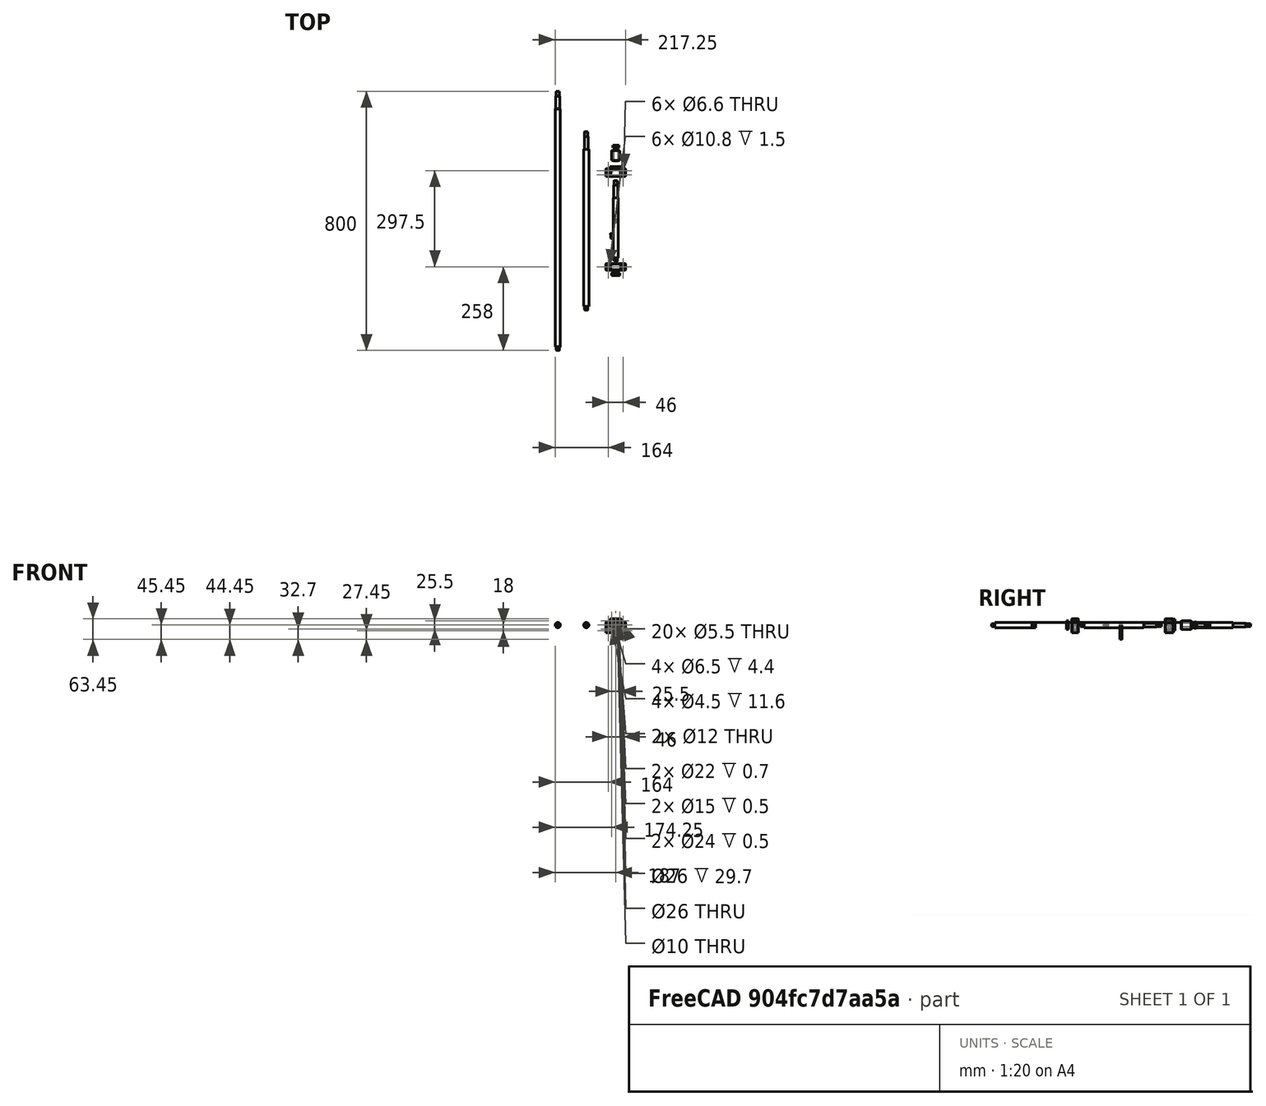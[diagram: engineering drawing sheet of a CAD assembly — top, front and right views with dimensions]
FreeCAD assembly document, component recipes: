
FREECAD ASSEMBLY — COMPONENT RECIPES ("Ballscrew")

This assembly document has 14 components, labeled P0..P13 below (a component is one placed body or linked part). 8 of them carry a construction recipe — the FreeCAD feature program that regenerates the part from scratch, quoted from this document or its linked companion documents; the rest are supplied as boundary geometry only. No exploded tour is included for this assembly.
COMPONENT P0 — recipe-attached ("Link(6000Z)", modeled in this document).
Construction recipe (the document's own serialized feature program — sketch geometry with constraints, then the solid features built on it; lengths are millimeters unless a unit is written):

FEATURE [Sketcher::SketchObject] Sketch002
  FullyConstrained = true
  MapMode = 5
  Placement = pos=(0,0,0) rot=(0.57735,0.57735,0.57735;2.0944rad)
  Support = -> [YZ_Plane001]
  sketch-geometry (21):
    g0: LineSegment StartX=-3.5 StartY=13 StartZ=0 EndX=3.5 EndY=13 EndZ=0
    g1: LineSegment StartX=3.5 StartY=13 StartZ=0 EndX=3.5 EndY=11 EndZ=0
    g2: LineSegment StartX=3.5 StartY=5 StartZ=0 EndX=-3.5 EndY=5 EndZ=0
    g3: LineSegment StartX=-3.5 StartY=5 StartZ=0 EndX=-3.5 EndY=7 EndZ=0
    g4: LineSegment StartX=-3.5 StartY=11 StartZ=0 EndX=-2.5 EndY=11 EndZ=0
    g5: LineSegment StartX=-2.5 StartY=11 StartZ=0 EndX=-2.5 EndY=10.5 EndZ=0
    g6: LineSegment StartX=-2.5 StartY=10.5 StartZ=0 EndX=-3 EndY=10.5 EndZ=0
    g7: LineSegment StartX=-3 StartY=10.5 StartZ=0 EndX=-3 EndY=7.5 EndZ=0
    g8: LineSegment StartX=-3 StartY=7.5 StartZ=0 EndX=-2.5 EndY=7.5 EndZ=0
    g9: LineSegment StartX=-2.5 StartY=7.5 StartZ=0 EndX=-2.5 EndY=7 EndZ=0
    g10: LineSegment StartX=-2.5 StartY=7 StartZ=0 EndX=-3.5 EndY=7 EndZ=0
    g11: LineSegment StartX=-3.5 StartY=11 StartZ=0 EndX=-3.5 EndY=13 EndZ=0
    g12: LineSegment StartX=3.5 StartY=11 StartZ=0 EndX=2.5 EndY=11 EndZ=0
    g13: LineSegment StartX=2.5 StartY=11 StartZ=0 EndX=2.5 EndY=10.5 EndZ=0
    g14: LineSegment StartX=2.5 StartY=10.5 StartZ=0 EndX=3 EndY=10.5 EndZ=0
    g15: LineSegment StartX=3 StartY=10.5 StartZ=0 EndX=3 EndY=7.5 EndZ=0
    g16: LineSegment StartX=3 StartY=7.5 StartZ=0 EndX=2.5 EndY=7.5 EndZ=0
    g17: LineSegment StartX=2.5 StartY=7.5 StartZ=0 EndX=2.5 EndY=7 EndZ=0
    g18: LineSegment StartX=2.5 StartY=7 StartZ=0 EndX=3.5 EndY=7 EndZ=0
    g19: LineSegment StartX=3.5 StartY=7 StartZ=0 EndX=3.5 EndY=5 EndZ=0
    g20: GeomPoint [constr] X=0 Y=5 Z=0
  constraints (59):
    c: Coincident(g0,g1)
    c: Coincident(g19,g2)
    c: Coincident(g2,g3)
    c: Coincident(g11,g0)
    c: Horizontal(g0)
    c: Horizontal(g2)
    c: Vertical(g1)
    c: Vertical(g3)
    c: DistanceX(g2,g2) = 7
    c: DistanceY(g-1,g0) = 13
    c: Horizontal(g4)
    c: Coincident(g4,g5)
    c: Coincident(g5,g6)
    c: Coincident(g6,g7)
    c: Vertical(g7)
    c: Coincident(g7,g8)
    c: Horizontal(g8)
    c: Coincident(g8,g9)
    c: Vertical(g9)
    c: Coincident(g9,g10)
    c: Horizontal(g10)
    c: Coincident(g3,g10)
    c: Coincident(g11,g4)
    c: Tangent(g3,g11)
    c: Equal(g8,g6)
    c: Horizontal(g6)
    c: Vertical(g5)
    c: Equal(g5,g9)
    c: DistanceX(g6,g6) = 0.5
    c: DistanceX(g4,g4) = 1
    c: Equal(g3,g11)
    c: DistanceY(g11,g11) = 2
    c: DistanceY(g5,g5) = 0.5
    c: Horizontal(g12)
    c: Coincident(g12,g13)
    c: Vertical(g13)
    c: Coincident(g13,g14)
    c: Coincident(g14,g15)
    c: Vertical(g15)
    c: Coincident(g15,g16)
    c: Horizontal(g16)
    c: Coincident(g16,g17)
    c: Vertical(g17)
    c: Coincident(g17,g18)
    c: Horizontal(g18)
    c: Coincident(g1,g12)
    c: Coincident(g19,g18)
    c: Tangent(g1,g19)
    c: Equal(g12,g4)
    c: Equal(g4,g18)
    c: Equal(g16,g14)
    c: Equal(g14,g6)
    c: Equal(g13,g17)
    c: Equal(g17,g9)
    c: Horizontal(g17,g9)
    c: Horizontal(g12,g4)
    c: PointOnObject(g20,g-2)
    c: Symmetric(g2,g2,g20)
    c: DistanceY(g-1,g2) = 5
FEATURE [PartDesign::Revolution] Revolution
  Angle = 360
  Axis = (1e-16,1,-1e-16)
  Base = (0,0,0)
  ClaimChildren = false
  Fit = 0
  FitJoin = 0
  InnerFit = 0
  InnerFitJoin = 0
  NewSolid = false
  Placement = pos=(0,0,0) rot=(0.57735,0.57735,0.57735;2.0944rad)
  Profile = -> Sketch002
  ReferenceAxis = -> Y_Axis001
  Refine = true
  Suppress = false
FEATURE [PartDesign::Chamfer] Chamfer001
  Angle = 45
  Base = -> Revolution [Edge2,Edge3,Edge18,Edge17,Edge15,Edge5,Edge1,Edge20]
  BaseFeature = -> Revolution
  ChamferType = 0
  FlipDirection = false
  NewSolid = false
  Placement = pos=(0,0,0) rot=(0.57735,0.57735,0.57735;2.0944rad)
  Refine = true
  Size = 0.3
  Size2 = 1
  SupportTransform = false
  Suppress = false
FEATURE [PartDesign::Body] Body001  label="6000Z"
  AutoGroupSolids = false
  ExportMode = 0
  Group = -> [Sketch002,Revolution,Chamfer001]
  Origin = -> Origin001
  Placement = pos=(0,-165,0) rot=(0,0,1;0rad)
  Tip = -> Chamfer001
  _ExportChildren = -> [Revolution,Chamfer001]
  _GroupVersion = 1
COMPONENT P1 — recipe-attached ("Link001(BF12)", modeled in this document).
Construction recipe (the document's own serialized feature program — sketch geometry with constraints, then the solid features built on it; lengths are millimeters unless a unit is written):

FEATURE [Sketcher::SketchObject] Sketch
  FullyConstrained = true
  MapMode = 5
  Placement = pos=(0,0,0) rot=(1,0,0;1.5708rad)
  Support = -> [XZ_Plane]
  sketch-geometry (18):
    g0: LineSegment StartX=-30.25 StartY=33 StartZ=0 EndX=-16.75 EndY=33 EndZ=0
    g1: LineSegment StartX=30.25 StartY=33 StartZ=0 EndX=30.25 EndY=0 EndZ=0
    g2: LineSegment StartX=30.25 StartY=0 StartZ=0 EndX=-30.25 EndY=0 EndZ=0
    g3: LineSegment StartX=-30.25 StartY=0 StartZ=0 EndX=-30.25 EndY=33 EndZ=0
    g4: LineSegment StartX=-16.75 StartY=43 StartZ=0 EndX=16.75 EndY=43 EndZ=0
    g5: LineSegment StartX=16.75 StartY=43 StartZ=0 EndX=16.75 EndY=33 EndZ=0
    g6: LineSegment StartX=-16.75 StartY=33 StartZ=0 EndX=-16.75 EndY=43 EndZ=0
    g7: Circle CenterX=-23 CenterY=25 CenterZ=0 NormalX=0 NormalY=0 NormalZ=1 AngleXU=0 Radius=2.75
    g8: Circle CenterX=-23 CenterY=7 CenterZ=0 NormalX=0 NormalY=0 NormalZ=1 AngleXU=0 Radius=2.75
    g9: Circle CenterX=23 CenterY=25 CenterZ=0 NormalX=0 NormalY=0 NormalZ=1 AngleXU=0 Radius=2.75
    g10: Circle CenterX=23 CenterY=7 CenterZ=0 NormalX=0 NormalY=0 NormalZ=1 AngleXU=0 Radius=2.75
    g11: LineSegment [constr] StartX=-23 StartY=25 StartZ=0 EndX=-23 EndY=7 EndZ=0
    g12: LineSegment [constr] StartX=23 StartY=25 StartZ=0 EndX=23 EndY=7 EndZ=0
    g13: LineSegment StartX=16.75 StartY=33 StartZ=0 EndX=30.25 EndY=33 EndZ=0
    g14: GeomPoint [constr] X=0 Y=43 Z=0
    g15: Circle CenterX=0 CenterY=25 CenterZ=0 NormalX=0 NormalY=0 NormalZ=1 AngleXU=0 Radius=13
    g16: GeomPoint [constr] X=0 Y=0 Z=0
    g17: GeomPoint [constr] X=0 Y=7 Z=0
  constraints (44):
    c: Coincident(g13,g1)
    c: Coincident(g1,g2)
    c: Coincident(g2,g3)
    c: Coincident(g3,g0)
    c: Horizontal(g0)
    c: Horizontal(g2)
    c: Vertical(g1)
    c: Vertical(g3)
    c: Coincident(g4,g5)
    c: Coincident(g6,g4)
    c: Horizontal(g4)
    c: Vertical(g5)
    c: Vertical(g6)
    c: Vertical(g8,g7)
    c: Vertical(g9,g10)
    c: Horizontal(g7,g9)
    c: Coincident(g11,g7)
    c: Coincident(g11,g8)
    c: Coincident(g12,g9)
    c: Coincident(g12,g10)
    c: Equal(g11,g12)
    c: Coincident(g13,g5)
    c: Tangent(g0,g13)
    c: Equal(g10,g9)
    c: Equal(g9,g7)
    c: Equal(g7,g8)
    c: PointOnObject(g14,g-2)
    c: Symmetric(g4,g4,g14)
    c: DistanceX(g2,g2) = 60.5
    c: DistanceX(g8,g10) = 46
    c: DistanceX(g4,g4) = 33.5
    c: DistanceY(g1,g4) = 43
    c: DistanceY(g1,g1) = 33
    c: PointOnObject(g15,g-2)
    c: DistanceY(g1,g15) = 25
    c: Horizontal(g15,g7)
    c: DistanceY(g11,g11) = 18
    c: Diameter(g7) = 5.5
    c: Symmetric(g2,g1,g16)
    c: Coincident(g6,g0)
    c: Coincident(g16,g-1)
    c: PointOnObject(g17,g-2)
    c: Symmetric(g8,g10,g17)
    c: Diameter(g15) = 26
FEATURE [PartDesign::Pad] Pad
  ClaimChildren = false
  Direction = (1,1,1)
  Fit = 0
  FitJoin = 0
  InnerFit = 0
  InnerFitJoin = 0
  InnerTaperAngle = 0
  InnerTaperAngleRev = 0
  Length = 20
  Length2 = 100
  Linearize = true
  Midplane = true
  NewSolid = false
  Placement = pos=(0,0,0) rot=(1,0,0;1.5708rad)
  Profile = -> Sketch
  Refine = true
  Suppress = false
  Type = 0
FEATURE [Sketcher::SketchObject] Sketch001
  FullyConstrained = true
  MapMode = 5
  Placement = pos=(0,0,0) rot=(1,0,0;3.14159rad)
  Support = -> [Pad]
  sketch-geometry (1):
    g0: Circle CenterX=-23 CenterY=0 CenterZ=0 NormalX=0 NormalY=0 NormalZ=1 AngleXU=0 Radius=3.3
  constraints (3):
    c: PointOnObject(g0,g-1)
    c: Diameter(g0) = 6.6
    c: DistanceX(g0,g-1) = 23
FEATURE [PartDesign::Pocket] Pocket
  BaseFeature = -> Pad
  ClaimChildren = false
  Fit = 0
  FitJoin = 0
  InnerFit = 0
  InnerFitJoin = 0
  InnerTaperAngle = 0
  InnerTaperAngleRev = 0
  Length = 5
  Length2 = 100
  Linearize = true
  NewSolid = false
  Placement = pos=(0,0,0) rot=(1,0,0;1.5708rad)
  Profile = -> Sketch001
  Refine = true
  Suppress = false
  Type = 1
FEATURE [PartDesign::Hole] Hole
  BaseFeature = -> Pocket
  ClaimChildren = false
  CustomThreadClearance = 0
  Depth = 25
  DepthType = 1
  Diameter = 6.6
  DrillForDepth = false
  DrillPoint = 1
  DrillPointAngle = 118
  Fit = 0
  FitJoin = 0
  HoleCutCountersinkAngle = 90
  HoleCutCustomValues = false
  HoleCutDepth = 1.5
  HoleCutDiameter = 10.8
  HoleCutType = 1
  InnerFit = 0
  InnerFitJoin = 0
  ModelThread = false
  NewSolid = false
  Placement = pos=(0,0,0) rot=(1,0,0;1.5708rad)
  Profile = -> Pocket [Edge5]
  Refine = true
  Suppress = false
  Tapered = false
  TaperedAngle = 90
  ThreadClass = 0
  ThreadDepth = 154.49
  ThreadDepthType = 0
  ThreadDirection = 0
  ThreadFit = 0
  ThreadSize = 0
  ThreadType = 0
  Threaded = false
  UseCustomThreadClearance = false
FEATURE [PartDesign::Mirrored] Mirrored
  BaseFeature = -> Hole
  CopyShape = false
  MirrorPlane = -> YZ_Plane
  NewSolid = false
  OriginalSubs = -> [Hole]
  Originals = -> [Hole]
  ParallelTransform = true
  Placement = pos=(0,0,0) rot=(1,0,0;1.5708rad)
  Refine = true
  SubTransform = true
  Suppress = false
  _Version = 1
FEATURE [PartDesign::Chamfer] Chamfer
  Angle = 45
  Base = -> Mirrored [Edge31,Edge37,Edge39,Edge34,Edge3,Edge23,Edge22,Edge21,Edge24,Edge25,Edge27,Edge29,Edge30,Edge28,Edge8,Edge6,Edge7,Edge2,Edge9,Edge1,Edge12,Edge11,Edge14,Edge17,Edge19,Edge18,Edge16,Edge15,Edge26,Edge36,Edge35,Edge10,Edge20,Edge13]
  BaseFeature = -> Mirrored
  ChamferType = 0
  FlipDirection = false
  NewSolid = false
  Placement = pos=(0,0,0) rot=(1,0,0;1.5708rad)
  Refine = true
  Size = 1
  Size2 = 1
  SupportTransform = false
  Suppress = false
FEATURE [PartDesign::Body] Body  label="BF12"
  AutoGroupSolids = false
  ExportMode = 0
  Group = -> [Sketch,Pad,Sketch001,Pocket,Hole,Mirrored,Chamfer]
  Origin = -> Origin
  Placement = pos=(0,-142,-24) rot=(0,0,1;0rad)
  Tip = -> Chamfer
  _ExportChildren = -> [Pad,Hole,Mirrored,Chamfer]
  _GroupVersion = 1
COMPONENT P2 — recipe-attached ("Link002(BK12 bearings)", modeled in this document).
Construction recipe (the document's own serialized feature program — sketch geometry with constraints, then the solid features built on it; lengths are millimeters unless a unit is written):

FEATURE [Sketcher::SketchObject] Sketch007
  FullyConstrained = true
  MapMode = 5
  Placement = pos=(0,0,0) rot=(0.57735,0.57735,0.57735;2.0944rad)
  Support = -> [YZ_Plane003]
  sketch-geometry (16):
    g0: LineSegment StartX=-15.5 StartY=13 StartZ=0 EndX=15.5 EndY=13 EndZ=0
    g1: LineSegment StartX=16 StartY=8 StartZ=0 EndX=16 EndY=6 EndZ=0
    g2: LineSegment StartX=16 StartY=6 StartZ=0 EndX=-16 EndY=6 EndZ=0
    g3: LineSegment StartX=-16 StartY=6 StartZ=0 EndX=-16 EndY=8 EndZ=0
    g4: LineSegment StartX=-15.5 StartY=13 StartZ=0 EndX=-15.5 EndY=12 EndZ=0
    g5: LineSegment StartX=-15.5 StartY=12 StartZ=0 EndX=-15 EndY=12 EndZ=0
    g6: LineSegment StartX=-15 StartY=12 StartZ=0 EndX=-15 EndY=9.5 EndZ=0
    g7: LineSegment StartX=-15 StartY=9.5 StartZ=0 EndX=-15.5 EndY=8.3 EndZ=0
    g8: LineSegment StartX=-15.5 StartY=8.3 StartZ=0 EndX=-15 EndY=8 EndZ=0
    g9: LineSegment StartX=-15 StartY=8 StartZ=0 EndX=-16 EndY=8 EndZ=0
    g10: LineSegment StartX=15.5 StartY=13 StartZ=0 EndX=15.5 EndY=12 EndZ=0
    g11: LineSegment StartX=15.5 StartY=12 StartZ=0 EndX=15 EndY=12 EndZ=0
    g12: LineSegment StartX=15 StartY=12 StartZ=0 EndX=15 EndY=9.5 EndZ=0
    g13: LineSegment StartX=15 StartY=9.5 StartZ=0 EndX=15.5 EndY=8.3 EndZ=0
    g14: LineSegment StartX=15.5 StartY=8.3 StartZ=0 EndX=15 EndY=8 EndZ=0
    g15: LineSegment StartX=15 StartY=8 StartZ=0 EndX=16 EndY=8 EndZ=0
  constraints (46):
    c: Coincident(g1,g2)
    c: Coincident(g2,g3)
    c: Vertical(g1)
    c: Vertical(g3)
    c: DistanceY(g-1,g1) = 6
    c: Vertical(g4)
    c: Coincident(g5,g4)
    c: Coincident(g6,g5)
    c: Vertical(g6)
    c: Coincident(g7,g6)
    c: Coincident(g8,g7)
    c: Coincident(g9,g8)
    c: Horizontal(g9)
    c: Coincident(g0,g4)
    c: Coincident(g3,g9)
    c: Coincident(g10,g11)
    c: Horizontal(g11)
    c: Coincident(g11,g12)
    c: Vertical(g12)
    c: Coincident(g12,g13)
    c: Coincident(g13,g14)
    c: Coincident(g14,g15)
    c: Horizontal(g15)
    c: Vertical(g10)
    c: Coincident(g1,g15)
    c: Coincident(g0,g10)
    c: Equal(g9,g15)
    c: Horizontal(g5)
    c: Equal(g5,g11)
    c: Equal(g12,g6)
    c: Equal(g7,g13)
    c: Equal(g8,g14)
    c: Symmetric(g1,g2,g-2)
    c: DistanceX(g2,g2) = 32
    c: Symmetric(g0,g0,g-2)
    c: DistanceX(g0,g0) = 31
    c: DistanceX(g5,g11) = 30
    c: DistanceX(g8,g14) = 30
    c: DistanceY(g14,g12) = 1.5
    c: DistanceY(g14,g13) = 0.3
    c: Equal(g10,g4)
    c: Horizontal(g13,g7)
    c: DistanceY(g3,g3) = 2
    c: DistanceX(g7,g13) = 31
    c: DistanceY(g4,g4) = 1
    c: DistanceY(g-1,g0) = 13
FEATURE [PartDesign::Revolution] Revolution001
  Angle = 360
  Axis = (1e-16,1,-1e-16)
  Base = (0,0,0)
  ClaimChildren = false
  Fit = 0
  FitJoin = 0
  InnerFit = 0
  InnerFitJoin = 0
  NewSolid = false
  Placement = pos=(0,0,0) rot=(0.57735,0.57735,0.57735;2.0944rad)
  Profile = -> Sketch007
  ReferenceAxis = -> Y_Axis003
  Refine = true
  Suppress = false
FEATURE [PartDesign::Chamfer] Chamfer003
  Angle = 45
  Base = -> Revolution001 [Edge15,Edge13,Edge3,Edge1,Edge16,Edge18]
  BaseFeature = -> Revolution001
  ChamferType = 0
  FlipDirection = false
  NewSolid = false
  Placement = pos=(0,0,0) rot=(0.57735,0.57735,0.57735;2.0944rad)
  Refine = true
  Size = 0.5
  Size2 = 1
  SupportTransform = false
  Suppress = false
FEATURE [PartDesign::Body] Body003  label="BK12 bearings"
  AutoGroupSolids = false
  ExportMode = 0
  Group = -> [Sketch007,Revolution001,Chamfer003]
  Origin = -> Origin003
  Placement = pos=(0,202,0) rot=(0,0,1;0rad)
  Tip = -> Chamfer003
  _ExportChildren = -> [Revolution001,Chamfer003]
  _GroupVersion = 1
COMPONENT P3 — recipe-attached ("Link003(BK12)", modeled in this document).
Construction recipe (the document's own serialized feature program — sketch geometry with constraints, then the solid features built on it; lengths are millimeters unless a unit is written):

FEATURE [Sketcher::SketchObject] Sketch003
  FullyConstrained = true
  MapMode = 5
  Placement = pos=(0,0,0) rot=(1,0,0;1.5708rad)
  Support = -> [XZ_Plane002]
  sketch-geometry (14):
    g0: LineSegment StartX=-30 StartY=32.5 StartZ=0 EndX=-16.75 EndY=32.5 EndZ=0
    g1: LineSegment StartX=30 StartY=32.5 StartZ=0 EndX=30 EndY=0 EndZ=0
    g2: LineSegment StartX=30 StartY=0 StartZ=0 EndX=-30 EndY=0 EndZ=0
    g3: LineSegment StartX=-30 StartY=0 StartZ=0 EndX=-30 EndY=32.5 EndZ=0
    g4: LineSegment StartX=-16.75 StartY=43 StartZ=0 EndX=16.75 EndY=43 EndZ=0
    g5: LineSegment StartX=16.75 StartY=43 StartZ=0 EndX=16.75 EndY=32.5 EndZ=0
    g6: LineSegment StartX=-16.75 StartY=32.5 StartZ=0 EndX=-16.75 EndY=43 EndZ=0
    g7: Circle CenterX=0 CenterY=25 CenterZ=0 NormalX=0 NormalY=0 NormalZ=1 AngleXU=0 Radius=13
    g8: Circle CenterX=-23 CenterY=25 CenterZ=0 NormalX=0 NormalY=0 NormalZ=1 AngleXU=0 Radius=2.75
    g9: Circle CenterX=-23 CenterY=7 CenterZ=0 NormalX=0 NormalY=0 NormalZ=1 AngleXU=0 Radius=2.75
    g10: Circle CenterX=23 CenterY=25 CenterZ=0 NormalX=0 NormalY=0 NormalZ=1 AngleXU=0 Radius=2.75
    g11: Circle CenterX=23 CenterY=7 CenterZ=0 NormalX=0 NormalY=0 NormalZ=1 AngleXU=0 Radius=2.75
    g12: LineSegment StartX=16.75 StartY=32.5 StartZ=0 EndX=30 EndY=32.5 EndZ=0
    g13: GeomPoint [constr] X=0 Y=0 Z=0
  constraints (37):
    c: Coincident(g12,g1)
    c: Coincident(g1,g2)
    c: Coincident(g2,g3)
    c: Coincident(g3,g0)
    c: Horizontal(g0)
    c: Horizontal(g2)
    c: Vertical(g1)
    c: Vertical(g3)
    c: Coincident(g4,g5)
    c: Coincident(g6,g4)
    c: Horizontal(g4)
    c: Vertical(g5)
    c: Vertical(g6)
    c: PointOnObject(g7,g-2)
    c: Vertical(g11,g10)
    c: Vertical(g8,g9)
    c: Horizontal(g8,g10)
    c: Horizontal(g7,g8)
    c: Tangent(g0,g12)
    c: Coincident(g6,g0)
    c: Coincident(g5,g12)
    c: Equal(g12,g0)
    c: Symmetric(g1,g2,g13)
    c: DistanceX(g2,g2) = 60
    c: DistanceX(g4,g4) = 33.5
    c: DistanceY(g1,g1) = 32.5
    c: DistanceY(g1,g4) = 43
    c: DistanceY(g11,g10) = 18
    c: DistanceX(g9,g11) = 46
    c: DistanceY(g1,g10) = 25
    c: Symmetric(g11,g9,g-2)
    c: Equal(g8,g10)
    c: Equal(g10,g11)
    c: Equal(g11,g9)
    c: Diameter(g8) = 5.5
    c: Diameter(g7) = 26
    c: Coincident(g13,g-1)
FEATURE [PartDesign::Pad] Pad001
  ClaimChildren = false
  Direction = (1,1,1)
  Fit = 0
  FitJoin = 0
  InnerFit = 0
  InnerFitJoin = 0
  InnerTaperAngle = 0
  InnerTaperAngleRev = 0
  Length = 24.7
  Length2 = 100
  Linearize = true
  Midplane = true
  NewSolid = false
  Placement = pos=(0,0,0) rot=(1,0,0;1.5708rad)
  Profile = -> Sketch003
  Refine = true
  Suppress = false
  Type = 0
FEATURE [Sketcher::SketchObject] Sketch004
  FullyConstrained = true
  MapMode = 5
  Placement = pos=(0,1.43e-14,32.5) rot=(0,0,1;3.14159rad)
  Support = -> [Pad001]
  sketch-geometry (2):
    g0: Circle CenterX=-23 CenterY=6.5 CenterZ=0 NormalX=0 NormalY=0 NormalZ=1 AngleXU=0 Radius=3.3
    g1: Circle CenterX=-23 CenterY=-6.5 CenterZ=0 NormalX=0 NormalY=0 NormalZ=1 AngleXU=0 Radius=3.3
  constraints (5):
    c: Equal(g0,g1)
    c: DistanceX(g0,g-1) = 23
    c: Diameter(g0) = 6.6
    c: DistanceY(g1,g0) = 13
    c: Symmetric(g1,g0,g-1)
FEATURE [PartDesign::Chamfer] Chamfer002
  Angle = 45
  Base = -> Pad001 [Edge8,Edge5,Edge9,Edge3,Edge6,Edge12,Edge15,Edge14,Edge18,Edge35,Edge29,Edge32,Edge38,Edge23,Edge21,Edge19,Edge16,Edge13,Edge10,Edge7,Edge4,Edge24,Edge27,Edge39,Edge33,Edge22,Edge17,Edge20,Edge1,Edge36,Edge30]
  BaseFeature = -> Pad001
  ChamferType = 0
  FlipDirection = false
  NewSolid = false
  Placement = pos=(0,0,0) rot=(1,0,0;1.5708rad)
  Refine = true
  Size = 1
  Size2 = 1
  SupportTransform = false
  Suppress = false
FEATURE [PartDesign::Hole] Hole001
  BaseFeature = -> Chamfer002
  ClaimChildren = false
  CustomThreadClearance = 0
  Depth = 25
  DepthType = 1
  Diameter = 6.6
  DrillForDepth = false
  DrillPoint = 1
  DrillPointAngle = 118
  Fit = 0
  FitJoin = 0
  HoleCutCountersinkAngle = 90
  HoleCutCustomValues = false
  HoleCutDepth = 1.5
  HoleCutDiameter = 10.8
  HoleCutType = 1
  InnerFit = 0
  InnerFitJoin = 0
  ModelThread = false
  NewSolid = false
  Placement = pos=(0,0,0) rot=(1,0,0;1.5708rad)
  Profile = -> Sketch004
  Refine = true
  Suppress = false
  Tapered = false
  TaperedAngle = 90
  ThreadClass = 0
  ThreadDepth = 157.24
  ThreadDepthType = 0
  ThreadDirection = 0
  ThreadFit = 0
  ThreadSize = 0
  ThreadType = 0
  Threaded = false
  UseCustomThreadClearance = false
FEATURE [PartDesign::Mirrored] Mirrored001
  BaseFeature = -> Hole001
  CopyShape = false
  MirrorPlane = -> YZ_Plane002
  NewSolid = false
  OriginalSubs = -> [Hole001]
  Originals = -> [Hole001]
  ParallelTransform = true
  Placement = pos=(0,0,0) rot=(1,0,0;1.5708rad)
  Refine = true
  SubTransform = true
  Suppress = false
  _Version = 1
FEATURE [Sketcher::SketchObject] Sketch005
  ExternalGeometry = -> [Mirrored001]
  FullyConstrained = true
  MapMode = 5
  Placement = pos=(0,12.35,-2.7e-15) rot=(-1,0,0;1.5708rad)
  Support = -> [Mirrored001]
  sketch-geometry (11):
    g0: LineSegment StartX=-13.75 StartY=-7.25 StartZ=0 EndX=13.75 EndY=-7.25 EndZ=0
    g1: LineSegment StartX=17.75 StartY=-11.25 StartZ=0 EndX=17.75 EndY=-38.75 EndZ=0
    g2: LineSegment StartX=13.75 StartY=-42.75 StartZ=0 EndX=-13.75 EndY=-42.75 EndZ=0
    g3: LineSegment StartX=-17.75 StartY=-38.75 StartZ=0 EndX=-17.75 EndY=-11.25 EndZ=0
    g4: LineSegment StartX=-17.75 StartY=-11.25 StartZ=0 EndX=-13.75 EndY=-7.25 EndZ=0
    g5: LineSegment StartX=13.75 StartY=-7.25 StartZ=0 EndX=17.75 EndY=-11.25 EndZ=0
    g6: LineSegment StartX=13.75 StartY=-42.75 StartZ=0 EndX=17.75 EndY=-38.75 EndZ=0
    g7: LineSegment StartX=-13.75 StartY=-42.75 StartZ=0 EndX=-17.75 EndY=-38.75 EndZ=0
    g8: GeomPoint [constr] X=-17.75 Y=-7.25 Z=0
    g9: GeomPoint [constr] X=17.75 Y=-42.75 Z=0
    g10: Circle CenterX=0 CenterY=-25 CenterZ=0 NormalX=0 NormalY=0 NormalZ=1 AngleXU=0 Radius=13
  constraints (29):
    c: Horizontal(g0)
    c: Horizontal(g2)
    c: Vertical(g1)
    c: Vertical(g3)
    c: Equal(g6,g7)
    c: Equal(g7,g4)
    c: Equal(g4,g5)
    c: Coincident(g0,g4)
    c: Coincident(g3,g4)
    c: Coincident(g0,g5)
    c: Coincident(g1,g5)
    c: Coincident(g1,g6)
    c: Coincident(g2,g6)
    c: Coincident(g2,g7)
    c: Coincident(g3,g7)
    c: Equal(g1,g0)
    c: Equal(g0,g3)
    c: Equal(g3,g2)
    c: Vertical(g0,g2)
    c: Vertical(g9,g1)
    c: Horizontal(g9,g2)
    c: Vertical(g8,g3)
    c: Horizontal(g8,g0)
    c: DistanceX(g3,g1) = 35.5
    c: Angle(g-2,g4) = 2.35619
    c: Diameter(g10) = 26
    c: DistanceX(g3,g0) = 4
    c: Coincident(g10,g-3)
    c: Symmetric(g8,g9,g10)
FEATURE [PartDesign::Pad] Pad002
  BaseFeature = -> Mirrored001
  ClaimChildren = false
  Direction = (1,1,1)
  Fit = 0
  FitJoin = 0
  InnerFit = 0
  InnerFitJoin = 0
  InnerTaperAngle = 0
  InnerTaperAngleRev = 0
  Length = 6
  Length2 = 100
  Linearize = true
  NewSolid = false
  Placement = pos=(0,0,0) rot=(1,0,0;1.5708rad)
  Profile = -> Sketch005
  Refine = true
  Suppress = false
  Type = 0
FEATURE [Sketcher::SketchObject] Sketch006
  ExternalGeometry = -> [Pad002]
  FullyConstrained = true
  MapMode = 5
  Placement = pos=(0,18.35,-2.02e-14) rot=(-1,0,0;1.5708rad)
  Support = -> [Pad002]
  sketch-geometry (4):
    g0: Circle CenterX=-12.75 CenterY=-12.25 CenterZ=0 NormalX=0 NormalY=0 NormalZ=1 AngleXU=0 Radius=2
    g1: Circle CenterX=12.75 CenterY=-12.25 CenterZ=0 NormalX=0 NormalY=0 NormalZ=1 AngleXU=0 Radius=2
    g2: Circle CenterX=12.75 CenterY=-37.75 CenterZ=0 NormalX=0 NormalY=0 NormalZ=1 AngleXU=0 Radius=2
    g3: Circle CenterX=-12.75 CenterY=-37.75 CenterZ=0 NormalX=0 NormalY=0 NormalZ=1 AngleXU=0 Radius=2
  constraints (11):
    c: Equal(g0,g1)
    c: Equal(g1,g2)
    c: Equal(g2,g3)
    c: Horizontal(g0,g1)
    c: Horizontal(g3,g2)
    c: Vertical(g0,g3)
    c: Vertical(g1,g2)
    c: Symmetric(g0,g2,g-3)
    c: Diameter(g0) = 4
    c: DistanceX(g0,g1) = 25.5
    c: DistanceY(g2,g1) = 25.5
FEATURE [PartDesign::Hole] Hole002
  BaseFeature = -> Pad002
  ClaimChildren = false
  CustomThreadClearance = 0
  Depth = 16
  DepthType = 0
  Diameter = 4.5
  DrillForDepth = false
  DrillPoint = 1
  DrillPointAngle = 118
  Fit = 0
  FitJoin = 0
  HoleCutCountersinkAngle = 90
  HoleCutCustomValues = false
  HoleCutDepth = 4.4
  HoleCutDiameter = 6.5
  HoleCutType = 1
  InnerFit = 0
  InnerFitJoin = 0
  ModelThread = false
  NewSolid = false
  Placement = pos=(0,0,0) rot=(1,0,0;1.5708rad)
  Profile = -> Sketch006
  Refine = true
  Suppress = false
  Tapered = false
  TaperedAngle = 90
  ThreadClass = 0
  ThreadDepth = 16
  ThreadDepthType = 0
  ThreadDirection = 0
  ThreadFit = 0
  ThreadSize = 11
  ThreadType = 1
  Threaded = false
  UseCustomThreadClearance = false
FEATURE [PartDesign::Chamfer] Chamfer007
  Angle = 45
  Base = -> Hole002 [Edge104,Edge149,Edge174,Edge173]
  BaseFeature = -> Hole002
  ChamferType = 0
  FlipDirection = false
  NewSolid = false
  Placement = pos=(0,0,0) rot=(1,0,0;1.5708rad)
  Refine = true
  Size = 1
  Size2 = 1
  SupportTransform = false
  Suppress = false
FEATURE [PartDesign::Body] Body002  label="BK12"
  AutoGroupSolids = false
  ExportMode = 0
  Group = -> [Sketch003,Pad001,Chamfer002,Sketch004,Hole001,Mirrored001,Sketch005,Pad002,Sketch006,Hole002,Chamfer007]
  Origin = -> Origin002
  Placement = pos=(0,149,-24) rot=(0,0,1;0rad)
  Tip = -> Chamfer007
  _ExportChildren = -> [Pad001,Chamfer002,Hole001,Mirrored001,Pad002,Hole002,Chamfer007]
  _GroupVersion = 1
COMPONENT P4 — geometry summary ("Link004(M4x12-Screw)"; no construction recipe available for this part):
  bounding box: 14.8 x 7.0 x 7.0 mm
  tessellated surface: 976 triangles
  volume: 241 mm^3 (33% of its bounding box)
  symmetry: 6-fold rotationally symmetric about the y axis; mirror-symmetric across its x mid-plane, z mid-plane
COMPONENT P5 — geometry summary ("Link005(M4x12-Screw)"; no construction recipe available for this part):
  bounding box: 14.8 x 7.0 x 7.0 mm
  tessellated surface: 976 triangles
  volume: 241 mm^3 (33% of its bounding box)
  symmetry: 6-fold rotationally symmetric about the y axis; mirror-symmetric across its x mid-plane, z mid-plane
COMPONENT P6 — geometry summary ("Link006(M4x12-Screw)"; no construction recipe available for this part):
  bounding box: 14.8 x 7.0 x 7.0 mm
  tessellated surface: 976 triangles
  volume: 241 mm^3 (33% of its bounding box)
  symmetry: 6-fold rotationally symmetric about the y axis; mirror-symmetric across its x mid-plane, z mid-plane
COMPONENT P7 — recipe-attached ("Link007(BK12 Nut)", modeled in this document).
Construction recipe (the document's own serialized feature program — sketch geometry with constraints, then the solid features built on it; lengths are millimeters unless a unit is written):

FEATURE [Sketcher::SketchObject] Sketch008
  FullyConstrained = true
  MapMode = 5
  Placement = pos=(0,0,0) rot=(1,0,0;1.5708rad)
  Support = -> [XZ_Plane004]
  sketch-geometry (11):
    g0: LineSegment StartX=-6.05635 StartY=9.5 StartZ=0 EndX=6.05635 EndY=9.5 EndZ=0
    g1: LineSegment StartX=9.5 StartY=6.05635 StartZ=0 EndX=9.5 EndY=-6.05635 EndZ=0
    g2: LineSegment StartX=6.05635 StartY=-9.5 StartZ=0 EndX=-6.05635 EndY=-9.5 EndZ=0
    g3: LineSegment StartX=-9.5 StartY=-6.05635 StartZ=0 EndX=-9.5 EndY=6.05635 EndZ=0
    g4: LineSegment StartX=-9.5 StartY=6.05635 StartZ=0 EndX=-6.05635 EndY=9.5 EndZ=0
    g5: LineSegment StartX=6.05635 StartY=9.5 StartZ=0 EndX=9.5 EndY=6.05635 EndZ=0
    g6: LineSegment StartX=6.05635 StartY=-9.5 StartZ=0 EndX=9.5 EndY=-6.05635 EndZ=0
    g7: LineSegment StartX=-9.5 StartY=-6.05635 StartZ=0 EndX=-6.05635 EndY=-9.5 EndZ=0
    g8: GeomPoint [constr] X=9.5 Y=9.5 Z=0
    g9: GeomPoint [constr] X=-9.5 Y=-9.5 Z=0
    g10: Circle CenterX=0 CenterY=0 CenterZ=0 NormalX=0 NormalY=0 NormalZ=1 AngleXU=0 Radius=6
  constraints (29):
    c: Horizontal(g0)
    c: Horizontal(g2)
    c: Vertical(g1)
    c: Vertical(g3)
    c: Parallel(g7,g5)
    c: Parallel(g4,g6)
    c: Equal(g5,g4)
    c: Equal(g4,g7)
    c: Equal(g7,g6)
    c: Angle(g4,g-2) = 0.785398
    c: Vertical(g5,g6)
    c: Coincident(g0,g4)
    c: Coincident(g3,g4)
    c: Coincident(g0,g5)
    c: Coincident(g1,g5)
    c: Coincident(g1,g6)
    c: Coincident(g2,g6)
    c: Coincident(g2,g7)
    c: Coincident(g3,g7)
    c: Horizontal(g9,g2)
    c: Vertical(g9,g3)
    c: Vertical(g8,g1)
    c: Horizontal(g0,g8)
    c: Symmetric(g9,g8,g-1)
    c: Equal(g3,g0)
    c: Distance(g1,g2) = 22
    c: DistanceX(g3,g1) = 19
    c: Coincident(g10,g-1)
    c: Diameter(g10) = 12
FEATURE [PartDesign::Pad] Pad003
  ClaimChildren = false
  Direction = (1,1,1)
  Fit = 0
  FitJoin = 0
  InnerFit = 0
  InnerFitJoin = 0
  InnerTaperAngle = 0
  InnerTaperAngleRev = 0
  Length = 7.2
  Length2 = 100
  Linearize = true
  Midplane = true
  NewSolid = false
  Placement = pos=(0,0,0) rot=(1,0,0;1.5708rad)
  Profile = -> Sketch008
  Refine = true
  Suppress = false
  Type = 0
FEATURE [Sketcher::SketchObject] Sketch009
  FullyConstrained = true
  MapMode = 5
  Placement = pos=(0,3.6,-8e-16) rot=(-1,0,0;1.5708rad)
  Support = -> [Pad003]
  sketch-geometry (2):
    g0: Circle CenterX=0 CenterY=0 CenterZ=0 NormalX=0 NormalY=0 NormalZ=1 AngleXU=0 Radius=8.75
    g1: Circle CenterX=0 CenterY=0 CenterZ=0 NormalX=0 NormalY=0 NormalZ=1 AngleXU=0 Radius=6
  constraints (4):
    c: Coincident(g0,g-1)
    c: Coincident(g1,g0)
    c: Diameter(g0) = 17.5
    c: Diameter(g1) = 12
FEATURE [PartDesign::Pad] Pad004
  BaseFeature = -> Pad003
  ClaimChildren = false
  Direction = (1,1,1)
  Fit = 0
  FitJoin = 0
  InnerFit = 0
  InnerFitJoin = 0
  InnerTaperAngle = 0
  InnerTaperAngleRev = 0
  Length = 0.5
  Length2 = 100
  Linearize = true
  NewSolid = false
  Placement = pos=(0,0,0) rot=(1,0,0;1.5708rad)
  Profile = -> Sketch009
  Refine = true
  Suppress = false
  Type = 0
FEATURE [Sketcher::SketchObject] Sketch010
  FullyConstrained = true
  MapMode = 5
  Placement = pos=(-7.77817,3.4e-15,7.77817) rot=(-0.382683,0,0.92388;3.14159rad)
  Support = -> [Pad004]
  sketch-geometry (1):
    g0: Circle CenterX=0 CenterY=0 CenterZ=0 NormalX=0 NormalY=0 NormalZ=1 AngleXU=0 Radius=1.5
  constraints (2):
    c: Coincident(g0,g-1)
    c: Diameter(g0) = 3
FEATURE [PartDesign::Pocket] Pocket001
  BaseFeature = -> Pad004
  ClaimChildren = false
  Fit = 0
  FitJoin = 0
  InnerFit = 0
  InnerFitJoin = 0
  InnerTaperAngle = 0
  InnerTaperAngleRev = 0
  Length = 5
  Length2 = 100
  Linearize = true
  NewSolid = false
  Placement = pos=(0,0,0) rot=(1,0,0;1.5708rad)
  Profile = -> Sketch010
  Refine = true
  Suppress = false
  Type = 2
FEATURE [PartDesign::Chamfer] Chamfer004
  Angle = 45
  Base = -> Pocket001 [Face5,Edge13,Edge8,Edge15,Edge16,Edge3,Edge6,Edge12,Edge14]
  BaseFeature = -> Pocket001
  ChamferType = 0
  FlipDirection = false
  NewSolid = false
  Placement = pos=(0,0,0) rot=(1,0,0;1.5708rad)
  Refine = true
  Size = 0.5
  Size2 = 1
  SupportTransform = false
  Suppress = false
FEATURE [PartDesign::Chamfer] Chamfer005
  Angle = 45
  Base = -> Chamfer004 [Edge67]
  BaseFeature = -> Chamfer004
  ChamferType = 0
  FlipDirection = false
  NewSolid = false
  Placement = pos=(0,0,0) rot=(1,0,0;1.5708rad)
  Refine = true
  Size = 1.5
  Size2 = 1
  SupportTransform = false
  Suppress = false
FEATURE [PartDesign::Body] Body004  label="BK12 Nut"
  AutoGroupSolids = false
  ExportMode = 0
  Group = -> [Sketch008,Pad003,Sketch009,Pad004,Sketch010,Pocket001,Chamfer004,Chamfer005]
  Origin = -> Origin004
  Placement = pos=(0,230,0) rot=(0,0,1;0rad)
  Tip = -> Chamfer005
  _ExportChildren = -> [Pad003,Pad004,Pocket001,Chamfer004,Chamfer005]
  _GroupVersion = 1
COMPONENT P8 — recipe-attached ("Link010(RM1605-250)", modeled in this document).
Construction recipe (the document's own serialized feature program — sketch geometry with constraints, then the solid features built on it; lengths are millimeters unless a unit is written):

FEATURE [Sketcher::SketchObject] Sketch011
  FullyConstrained = true
  MapMode = 5
  Placement = pos=(0,0,0) rot=(0.57735,0.57735,0.57735;2.0944rad)
  Support = -> [YZ_Plane005]
  sketch-geometry (14):
    g0: LineSegment StartX=-125 StartY=0 StartZ=0 EndX=125 EndY=0 EndZ=0
    g1: LineSegment StartX=125 StartY=0 StartZ=0 EndX=125 EndY=5 EndZ=0
    g2: LineSegment StartX=125 StartY=5 StartZ=0 EndX=110 EndY=5 EndZ=0
    g3: LineSegment StartX=110 StartY=5 StartZ=0 EndX=110 EndY=6 EndZ=0
    g4: LineSegment StartX=110 StartY=6 StartZ=0 EndX=71 EndY=6 EndZ=0
    g5: LineSegment StartX=71 StartY=6 StartZ=0 EndX=71 EndY=8 EndZ=0
    g6: LineSegment StartX=71 StartY=8 StartZ=0 EndX=-114 EndY=8 EndZ=0
    g7: LineSegment StartX=-114 StartY=8 StartZ=0 EndX=-114 EndY=5 EndZ=0
    g8: LineSegment StartX=-114 StartY=5 StartZ=0 EndX=-122.2 EndY=5 EndZ=0
    g9: LineSegment StartX=-122.2 StartY=5 StartZ=0 EndX=-122.2 EndY=4.6 EndZ=0
    g10: LineSegment StartX=-122.2 StartY=4.6 StartZ=0 EndX=-123.2 EndY=4.6 EndZ=0
    g11: LineSegment StartX=-123.2 StartY=4.6 StartZ=0 EndX=-123.2 EndY=5 EndZ=0
    g12: LineSegment StartX=-123.2 StartY=5 StartZ=0 EndX=-125 EndY=5 EndZ=0
    g13: LineSegment StartX=-125 StartY=5 StartZ=0 EndX=-125 EndY=0 EndZ=0
  constraints (41):
    c: PointOnObject(g0,g-1)
    c: Coincident(g0,g1)
    c: Vertical(g1)
    c: Coincident(g1,g2)
    c: Horizontal(g2)
    c: Coincident(g2,g3)
    c: Vertical(g3)
    c: Coincident(g3,g4)
    c: Horizontal(g4)
    c: Coincident(g4,g5)
    c: Vertical(g5)
    c: Coincident(g5,g6)
    c: Horizontal(g6)
    c: Coincident(g6,g7)
    c: Vertical(g7)
    c: Coincident(g7,g8)
    c: Horizontal(g8)
    c: Coincident(g8,g9)
    c: Vertical(g9)
    c: Coincident(g9,g10)
    c: Horizontal(g10)
    c: Coincident(g10,g11)
    c: Vertical(g11)
    c: Coincident(g11,g12)
    c: Horizontal(g12)
    c: Coincident(g12,g13)
    c: Coincident(g13,g0)
    c: DistanceY(g1,g1) = 5
    c: DistanceY(g0,g3) = 6
    c: DistanceY(g0,g5) = 8
    c: Vertical(g13)
    c: Horizontal(g11,g8)
    c: DistanceY(g0,g12) = 5
    c: DistanceY(g0,g9) = 4.6
    c: DistanceX(g10,g10) = 1
    c: DistanceX(g12,g12) = 1.8
    c: DistanceX(g0,g7) = 11
    c: DistanceX(g2,g2) = 15
    c: DistanceX(g5,g0) = 54
    c: DistanceX(g0,g0) = 250
    c: Symmetric(g0,g0,g-1)
FEATURE [PartDesign::Revolution] Revolution002
  Angle = 360
  Axis = (1e-16,1,-1e-16)
  Base = (0,0,0)
  ClaimChildren = false
  Fit = 0
  FitJoin = 0
  InnerFit = 0
  InnerFitJoin = 0
  NewSolid = false
  Placement = pos=(0,0,0) rot=(0.57735,0.57735,0.57735;2.0944rad)
  Profile = -> Sketch011
  ReferenceAxis = -> Y_Axis005
  Refine = true
  Suppress = false
FEATURE [PartDesign::Chamfer] Chamfer006
  Angle = 45
  Base = -> Revolution002 [Edge17,Edge1,Edge2,Edge5,Edge10]
  BaseFeature = -> Revolution002
  ChamferType = 0
  FlipDirection = false
  NewSolid = false
  Placement = pos=(0,0,0) rot=(0.57735,0.57735,0.57735;2.0944rad)
  Refine = true
  Size = 0.6
  Size2 = 1
  SupportTransform = false
  Suppress = false
FEATURE [PartDesign::Line] DatumLine
  AttacherType = Attacher::AttachEngineLine
  Length = 250
  MapMode = 19
  MinimumLength = 10
  Placement = pos=(7.9e-15,71,-2.31e-14) rot=(-0.57735,-0.57735,-0.57735;2.0944rad)
  ResizeMode = 0
  Support = -> [Chamfer006]
FEATURE [PartDesign::Body] Body005  label="RM1605-250"
  AutoGroupSolids = false
  ExportMode = 0
  Group = -> [Sketch011,Revolution002,Chamfer006,DatumLine]
  Origin = -> Origin005
  Tip = -> Chamfer006
  _ExportChildren = -> [Revolution002,Chamfer006,DatumLine]
  _GroupVersion = 1
COMPONENT P9 — recipe-attached ("Link013(RM1605-600)", modeled in this document).
Construction recipe (the document's own serialized feature program — sketch geometry with constraints, then the solid features built on it; lengths are millimeters unless a unit is written):

FEATURE [Sketcher::SketchObject] Sketch012
  FullyConstrained = true
  MapMode = 5
  Placement = pos=(0,0,0) rot=(0.57735,0.57735,0.57735;2.0944rad)
  Support = -> [YZ_Plane006]
  sketch-geometry (14):
    g0: LineSegment StartX=-275 StartY=0 StartZ=0 EndX=275 EndY=0 EndZ=0
    g1: LineSegment StartX=275 StartY=0 StartZ=0 EndX=275 EndY=5 EndZ=0
    g2: LineSegment StartX=275 StartY=5 StartZ=0 EndX=260 EndY=5 EndZ=0
    g3: LineSegment StartX=260 StartY=5 StartZ=0 EndX=260 EndY=6 EndZ=0
    g4: LineSegment StartX=260 StartY=6 StartZ=0 EndX=221 EndY=6 EndZ=0
    g5: LineSegment StartX=221 StartY=6 StartZ=0 EndX=221 EndY=8 EndZ=0
    g6: LineSegment StartX=221 StartY=8 StartZ=0 EndX=-264 EndY=8 EndZ=0
    g7: LineSegment StartX=-264 StartY=8 StartZ=0 EndX=-264 EndY=5 EndZ=0
    g8: LineSegment StartX=-264 StartY=5 StartZ=0 EndX=-272.2 EndY=5 EndZ=0
    g9: LineSegment StartX=-272.2 StartY=5 StartZ=0 EndX=-272.2 EndY=4.6 EndZ=0
    g10: LineSegment StartX=-272.2 StartY=4.6 StartZ=0 EndX=-273.2 EndY=4.6 EndZ=0
    g11: LineSegment StartX=-273.2 StartY=4.6 StartZ=0 EndX=-273.2 EndY=5 EndZ=0
    g12: LineSegment StartX=-273.2 StartY=5 StartZ=0 EndX=-275 EndY=5 EndZ=0
    g13: LineSegment StartX=-275 StartY=5 StartZ=0 EndX=-275 EndY=0 EndZ=0
  constraints (41):
    c: PointOnObject(g0,g-1)
    c: Coincident(g0,g1)
    c: Vertical(g1)
    c: Coincident(g1,g2)
    c: Horizontal(g2)
    c: Coincident(g2,g3)
    c: Vertical(g3)
    c: Coincident(g3,g4)
    c: Horizontal(g4)
    c: Coincident(g4,g5)
    c: Vertical(g5)
    c: Coincident(g5,g6)
    c: Horizontal(g6)
    c: Coincident(g6,g7)
    c: Vertical(g7)
    c: Coincident(g7,g8)
    c: Horizontal(g8)
    c: Coincident(g8,g9)
    c: Vertical(g9)
    c: Coincident(g9,g10)
    c: Horizontal(g10)
    c: Coincident(g10,g11)
    c: Vertical(g11)
    c: Coincident(g11,g12)
    c: Horizontal(g12)
    c: Coincident(g12,g13)
    c: Coincident(g13,g0)
    c: DistanceY(g1,g1) = 5
    c: DistanceY(g0,g3) = 6
    c: DistanceY(g0,g5) = 8
    c: Vertical(g13)
    c: Horizontal(g11,g8)
    c: DistanceY(g0,g12) = 5
    c: DistanceY(g0,g9) = 4.6
    c: DistanceX(g10,g10) = 1
    c: DistanceX(g12,g12) = 1.8
    c: DistanceX(g0,g7) = 11
    c: DistanceX(g2,g2) = 15
    c: DistanceX(g5,g0) = 54
    c: DistanceX(g0,g0) = 550
    c: Symmetric(g0,g0,g-1)
FEATURE [PartDesign::Revolution] Revolution003
  Angle = 360
  Axis = (1e-16,1,-1e-16)
  Base = (0,0,0)
  ClaimChildren = false
  Fit = 0
  FitJoin = 0
  InnerFit = 0
  InnerFitJoin = 0
  NewSolid = false
  Placement = pos=(0,0,0) rot=(0.57735,0.57735,0.57735;2.0944rad)
  Profile = -> Sketch012
  ReferenceAxis = -> Y_Axis006
  Refine = true
  Suppress = false
FEATURE [PartDesign::Chamfer] Chamfer008
  Angle = 45
  Base = -> Revolution003 [Edge1,Edge2,Edge5,Edge17,Edge10]
  BaseFeature = -> Revolution003
  ChamferType = 0
  FlipDirection = false
  NewSolid = false
  Placement = pos=(0,0,0) rot=(0.57735,0.57735,0.57735;2.0944rad)
  Refine = true
  Size = 0.5
  Size2 = 1
  SupportTransform = false
  Suppress = false
FEATURE [PartDesign::Line] DatumLine001
  AttacherType = Attacher::AttachEngineLine
  Length = 550
  MapMode = 19
  MinimumLength = 10
  Placement = pos=(2.45e-14,221,-7.28e-14) rot=(-0.57735,-0.57735,-0.57735;2.0944rad)
  ResizeMode = 0
  Support = -> [Chamfer008]
FEATURE [PartDesign::Body] Body006  label="RM1605-600"
  AutoGroupSolids = false
  ExportMode = 0
  Group = -> [Sketch012,Revolution003,Chamfer008,DatumLine001]
  Origin = -> Origin006
  Placement = pos=(-91,0,0) rot=(0,0,1;0rad)
  Tip = -> Chamfer008
  _ExportChildren = -> [Revolution003,Chamfer008,DatumLine001]
  _GroupVersion = 1
COMPONENT P10 — recipe-attached ("Link014(RM1605-800)", modeled in this document).
Construction recipe (the document's own serialized feature program — sketch geometry with constraints, then the solid features built on it; lengths are millimeters unless a unit is written):

FEATURE [Sketcher::SketchObject] Sketch013
  FullyConstrained = true
  MapMode = 5
  Placement = pos=(0,0,0) rot=(0.57735,0.57735,0.57735;2.0944rad)
  Support = -> [YZ_Plane007]
  sketch-geometry (14):
    g0: LineSegment StartX=-400 StartY=0 StartZ=0 EndX=400 EndY=0 EndZ=0
    g1: LineSegment StartX=400 StartY=0 StartZ=0 EndX=400 EndY=5 EndZ=0
    g2: LineSegment StartX=400 StartY=5 StartZ=0 EndX=385 EndY=5 EndZ=0
    g3: LineSegment StartX=385 StartY=5 StartZ=0 EndX=385 EndY=6 EndZ=0
    g4: LineSegment StartX=385 StartY=6 StartZ=0 EndX=346 EndY=6 EndZ=0
    g5: LineSegment StartX=346 StartY=6 StartZ=0 EndX=346 EndY=8 EndZ=0
    g6: LineSegment StartX=346 StartY=8 StartZ=0 EndX=-389 EndY=8 EndZ=0
    g7: LineSegment StartX=-389 StartY=8 StartZ=0 EndX=-389 EndY=5 EndZ=0
    g8: LineSegment StartX=-389 StartY=5 StartZ=0 EndX=-397.2 EndY=5 EndZ=0
    g9: LineSegment StartX=-397.2 StartY=5 StartZ=0 EndX=-397.2 EndY=4.6 EndZ=0
    g10: LineSegment StartX=-397.2 StartY=4.6 StartZ=0 EndX=-398.2 EndY=4.6 EndZ=0
    g11: LineSegment StartX=-398.2 StartY=4.6 StartZ=0 EndX=-398.2 EndY=5 EndZ=0
    g12: LineSegment StartX=-398.2 StartY=5 StartZ=0 EndX=-400 EndY=5 EndZ=0
    g13: LineSegment StartX=-400 StartY=5 StartZ=0 EndX=-400 EndY=0 EndZ=0
  constraints (41):
    c: PointOnObject(g0,g-1)
    c: Coincident(g0,g1)
    c: Vertical(g1)
    c: Coincident(g1,g2)
    c: Horizontal(g2)
    c: Coincident(g2,g3)
    c: Vertical(g3)
    c: Coincident(g3,g4)
    c: Horizontal(g4)
    c: Coincident(g4,g5)
    c: Vertical(g5)
    c: Coincident(g5,g6)
    c: Horizontal(g6)
    c: Coincident(g6,g7)
    c: Vertical(g7)
    c: Coincident(g7,g8)
    c: Horizontal(g8)
    c: Coincident(g8,g9)
    c: Vertical(g9)
    c: Coincident(g9,g10)
    c: Horizontal(g10)
    c: Coincident(g10,g11)
    c: Vertical(g11)
    c: Coincident(g11,g12)
    c: Horizontal(g12)
    c: Coincident(g12,g13)
    c: Coincident(g13,g0)
    c: DistanceY(g1,g1) = 5
    c: DistanceY(g0,g3) = 6
    c: DistanceY(g0,g5) = 8
    c: Vertical(g13)
    c: Horizontal(g11,g8)
    c: DistanceY(g0,g12) = 5
    c: DistanceY(g0,g9) = 4.6
    c: DistanceX(g10,g10) = 1
    c: DistanceX(g12,g12) = 1.8
    c: DistanceX(g0,g7) = 11
    c: DistanceX(g2,g2) = 15
    c: DistanceX(g5,g0) = 54
    c: DistanceX(g0,g0) = 800
    c: Symmetric(g0,g0,g-1)
FEATURE [PartDesign::Revolution] Revolution004
  Angle = 360
  Axis = (1e-16,1,-1e-16)
  Base = (0,0,0)
  ClaimChildren = false
  Fit = 0
  FitJoin = 0
  InnerFit = 0
  InnerFitJoin = 0
  NewSolid = false
  Placement = pos=(0,0,0) rot=(0.57735,0.57735,0.57735;2.0944rad)
  Profile = -> Sketch013
  ReferenceAxis = -> Y_Axis007
  Refine = true
  Suppress = false
FEATURE [PartDesign::Chamfer] Chamfer009
  Angle = 45
  Base = -> Revolution004 [Edge1,Edge5,Edge2,Edge17,Edge10]
  BaseFeature = -> Revolution004
  ChamferType = 0
  FlipDirection = false
  NewSolid = false
  Placement = pos=(0,0,0) rot=(0.57735,0.57735,0.57735;2.0944rad)
  Refine = true
  Size = 0.6
  Size2 = 1
  SupportTransform = false
  Suppress = false
FEATURE [PartDesign::Line] DatumLine002
  AttacherType = Attacher::AttachEngineLine
  Length = 800
  MapMode = 19
  MinimumLength = 10
  Placement = pos=(3.84e-14,346,-1.146e-13) rot=(-0.57735,-0.57735,-0.57735;2.0944rad)
  ResizeMode = 0
  Support = -> [Chamfer009]
FEATURE [PartDesign::Body] Body007  label="RM1605-800"
  AutoGroupSolids = false
  ExportMode = 0
  Group = -> [Sketch013,Revolution004,Chamfer009,DatumLine002]
  Origin = -> Origin007
  Placement = pos=(-179,0,0) rot=(0,0,1;0rad)
  Tip = -> Chamfer009
  _ExportChildren = -> [Revolution004,Chamfer009,DatumLine002]
  _GroupVersion = 1
COMPONENT P11 — geometry summary ("1/4inx1 3/4in-Screw 6ct"; no construction recipe available for this part):
  bounding box: 220.1 x 57.1 x 48.4 mm
  tessellated surface: 19,200 triangles
  volume: 9509 mm^3 (2% of its bounding box)
  symmetry: mirror-symmetric across its x mid-plane
COMPONENT P12 — geometry summary ("1/4inx1 3/4in-Screw 6ct  "; no construction recipe available for this part):
  bounding box: 519.7 x 57.1 x 48.4 mm
  tessellated surface: 19,200 triangles
  volume: 9509 mm^3 (1% of its bounding box)
  symmetry: mirror-symmetric across its x mid-plane
COMPONENT P13 — geometry summary ("1/4inx1 3/4in-Screw 6ct "; no construction recipe available for this part):
  bounding box: 769.7 x 57.1 x 48.4 mm
  tessellated surface: 19,200 triangles
  volume: 9509 mm^3 (0% of its bounding box)
  symmetry: 2-fold rotationally symmetric about the y axis; mirror-symmetric across its x mid-plane, z mid-plane
PROVENANCE & LICENSES
A FreeCAD (.FCStd) document from a public repository crawl; recipes are the document's own serialized feature recipes (and, for linked parts, companion documents' recipes).
License: mit.
